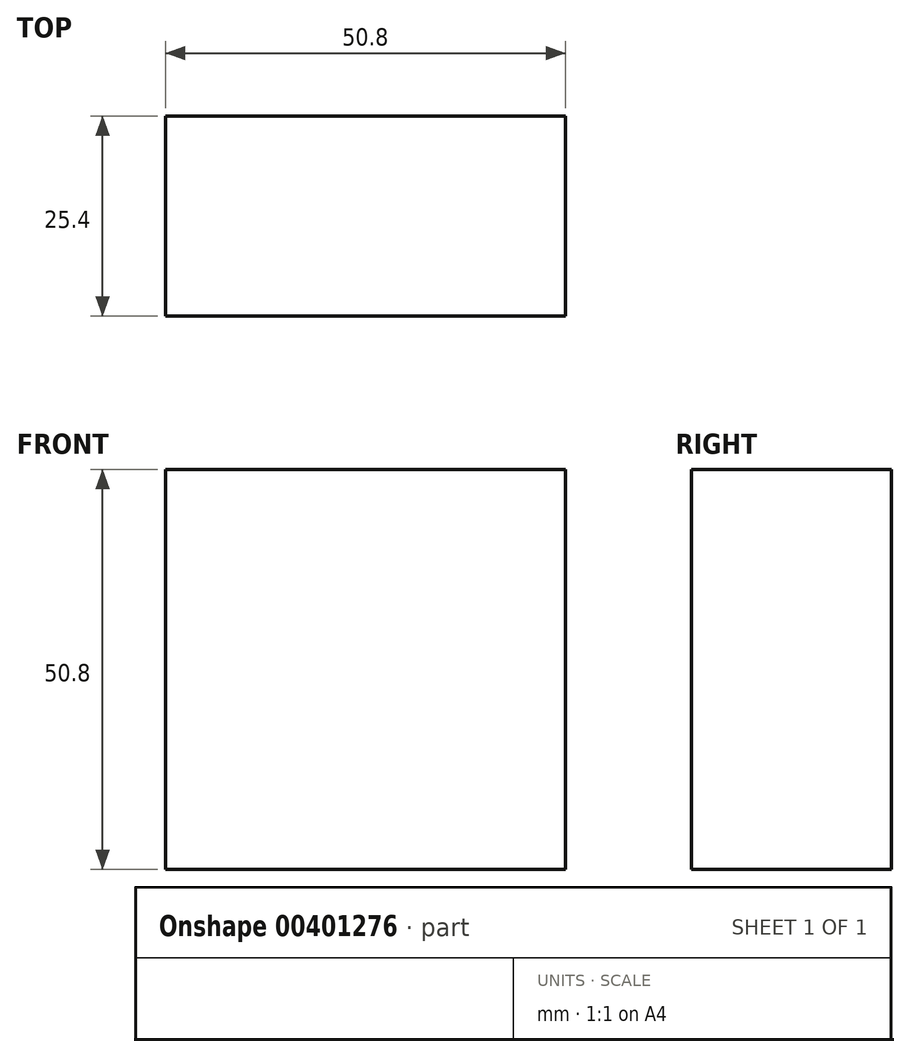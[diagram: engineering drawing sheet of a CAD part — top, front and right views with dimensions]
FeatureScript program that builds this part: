
annotation { "Feature Type Name" : "Feature", "Feature Type Description" : "" }
export const myFeature = defineFeature(function(context is Context, id is Id, definition is map)
    precondition{}
    {
        {
            var Q0;
            Q0=qCreatedBy(makeId("Front.planeOp"),FACE);
            var sketch = newSketch(context, id + "F0", { "sketchPlane" : qUnion([Q0])});
            skLineSegment(sketch, "E0.bottom", {"start": v(-66.45, 78.53) * mm, "end": v(-15.65, 78.53) * mm});
            skLineSegment(sketch, "E0.top", {"start": v(-66.45, 27.73) * mm, "end": v(-15.65, 27.73) * mm});
            skLineSegment(sketch, "E0.left", {"start": v(-66.45, 78.53) * mm, "end": v(-66.45, 27.73) * mm});
            skLineSegment(sketch, "E0.right", {"start": v(-15.65, 78.53) * mm, "end": v(-15.65, 27.73) * mm});
            skSolve(sketch);
        }
        {
            var Q0;
            Q0 = qSketchRegion(id + "F0", true);
            extrude(context, id + "F1", {"entities" : qUnion([Q0]), "depth" : 25.4 * mm});
        }
    });
